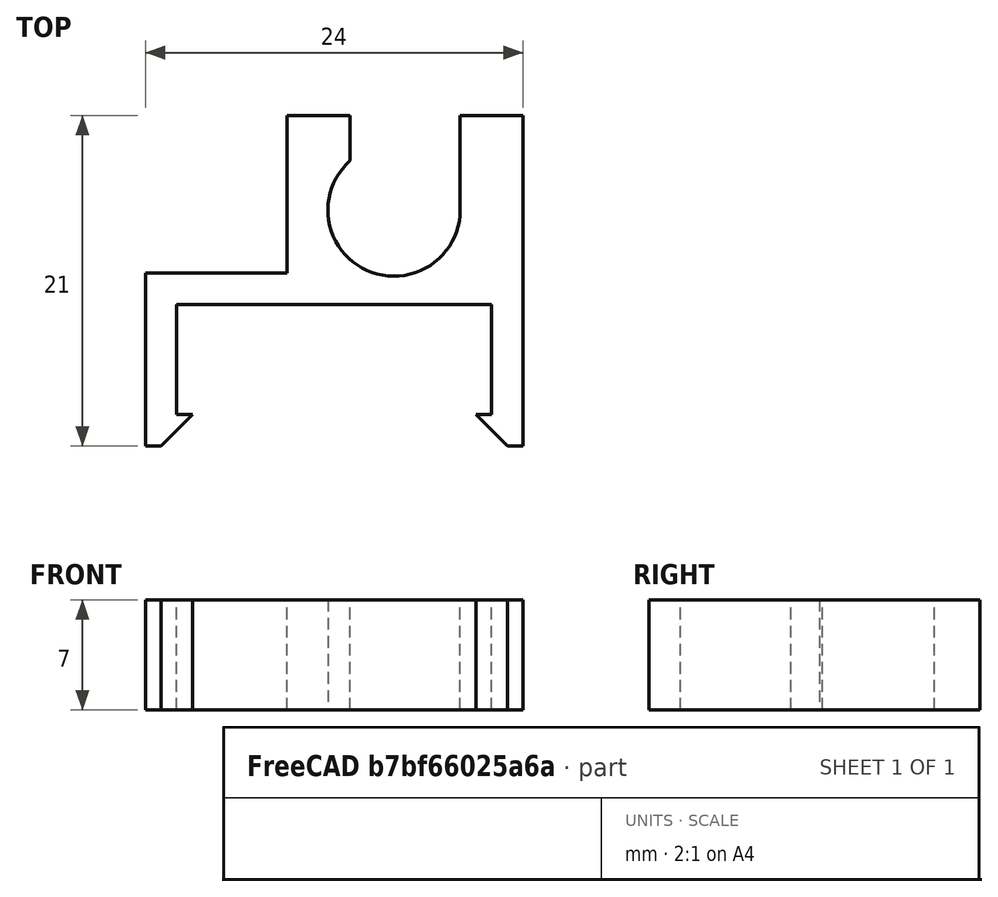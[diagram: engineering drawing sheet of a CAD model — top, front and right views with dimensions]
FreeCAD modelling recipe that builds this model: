
FCSTD DOCUMENT  (FreeCAD 0.18R16131 (Git))
Label: Endstopholder3
License: All rights reserved
LicenseURL: http://en.wikipedia.org/wiki/All_rights_reserved
objects: Sketcher::SketchObject×1, PartDesign::Pad×1, PartDesign::Body×1
note: 4 computed .brp shape members not serialized (recipe doc carries the construction recipe); baked Part::Feature solids carry a one-line shape summary decoded from their .brp

FEATURE [Sketcher::SketchObject] Sketch
  MapMode = 5
  Support = -> [XY_Plane]
  sketch-geometry (18):
    g0: ArcOfCircle CenterX=0 CenterY=-9e-16 CenterZ=0 NormalX=0 NormalY=0 NormalZ=1 AngleXU=0 Radius=4.2 StartAngle=2.30052 EndAngle=6.28319
    g1: LineSegment StartX=8.2 StartY=6 StartZ=0 EndX=8.2 EndY=-15 EndZ=0
    g2: LineSegment StartX=8.2 StartY=-15 StartZ=0 EndX=7.2 EndY=-15 EndZ=0
    g3: LineSegment StartX=7.2 StartY=-15 StartZ=0 EndX=5.2 EndY=-13 EndZ=0
    g4: LineSegment StartX=5.2 StartY=-13 StartZ=0 EndX=6.2 EndY=-13 EndZ=0
    g5: LineSegment StartX=6.2 StartY=-13 StartZ=0 EndX=6.2 EndY=-6 EndZ=0
    g6: LineSegment StartX=6.2 StartY=-6 StartZ=0 EndX=-13.8 EndY=-6 EndZ=0
    g7: LineSegment StartX=-13.8 StartY=-6 StartZ=0 EndX=-13.8 EndY=-13 EndZ=0
    g8: LineSegment StartX=-13.8 StartY=-13 StartZ=0 EndX=-12.8 EndY=-13 EndZ=0
    g9: LineSegment StartX=-12.8 StartY=-13 StartZ=0 EndX=-14.8 EndY=-15 EndZ=0
    g10: LineSegment StartX=-14.8 StartY=-15 StartZ=0 EndX=-15.8 EndY=-15 EndZ=0
    g11: LineSegment StartX=-15.8 StartY=-15 StartZ=0 EndX=-15.8 EndY=-4 EndZ=0
    g12: LineSegment StartX=-15.8 StartY=-4 StartZ=0 EndX=-6.8 EndY=-4 EndZ=0
    g13: LineSegment StartX=-6.8 StartY=-4 StartZ=0 EndX=-6.8 EndY=6 EndZ=0
    g14: LineSegment StartX=-6.8 StartY=6 StartZ=0 EndX=-2.8 EndY=6 EndZ=0
    g15: LineSegment StartX=-2.8 StartY=6 StartZ=0 EndX=-2.8 EndY=3.1305 EndZ=0
    g16: LineSegment StartX=4.2 StartY=6 StartZ=0 EndX=8.2 EndY=6 EndZ=0
    g17: LineSegment StartX=4.2 StartY=6 StartZ=0 EndX=4.2 EndY=-9e-16 EndZ=0
  constraints (54):
    c: Radius(g0) = 4.2
    c: Coincident(g1,g2)
    c: Coincident(g2,g3)
    c: Coincident(g3,g4)
    c: Coincident(g4,g5)
    c: Coincident(g5,g6)
    c: Coincident(g6,g7)
    c: Coincident(g7,g8)
    c: Coincident(g8,g9)
    c: Coincident(g9,g10)
    c: Coincident(g10,g11)
    c: Coincident(g11,g12)
    c: Coincident(g12,g13)
    c: Coincident(g13,g14)
    c: Coincident(g14,g15)
    c: Coincident(g16,g1)
    c: Horizontal(g16)
    c: Horizontal(g14)
    c: Horizontal(g12)
    c: Horizontal(g6)
    c: Horizontal(g10)
    c: Horizontal(g2)
    c: Vertical(g15)
    c: Vertical(g13)
    c: Vertical(g11)
    c: Vertical(g7)
    c: Vertical(g5)
    c: Vertical(g1)
    c: DistanceX(g14,g16) = 7
    c: DistanceX(g13,g1) = 15
    c: DistanceX(g16,g1) = 4
    c: DistanceY(g-1,g1) = 6
    c: DistanceY(g5,g-1) = 6
    c: DistanceY(g4,g5) = 7
    c: Horizontal(g4)
    c: DistanceX(g3,g4) = 1
    c: DistanceX(g4,g1) = 2
    c: DistanceX(g2,g1) = 1
    c: DistanceY(g1,g4) = 2
    c: Horizontal(g8,g3)
    c: Horizontal(g10,g1)
    c: Horizontal(g8)
    c: Equal(g10,g2)
    c: Equal(g8,g4)
    c: DistanceX(g10,g6) = 2
    c: DistanceX(g6,g5) = 20
    c: DistanceY(g6,g11) = 2
    c: Coincident(g15,g0)
    c: Coincident(g17,g0)
    c: Coincident(g0,g-1)
    c: Coincident(g17,g16)
    c: Vertical(g17)
    c: Horizontal(g0,g0)
    c: Horizontal(g14,g16)
FEATURE [PartDesign::Pad] Pad
  Length = 7
  Length2 = 100
  Profile = -> Sketch
  Type = 0
FEATURE [PartDesign::Body] Body
  Group = -> [Sketch,Pad]
  Origin = -> Origin
  Tip = -> Pad
